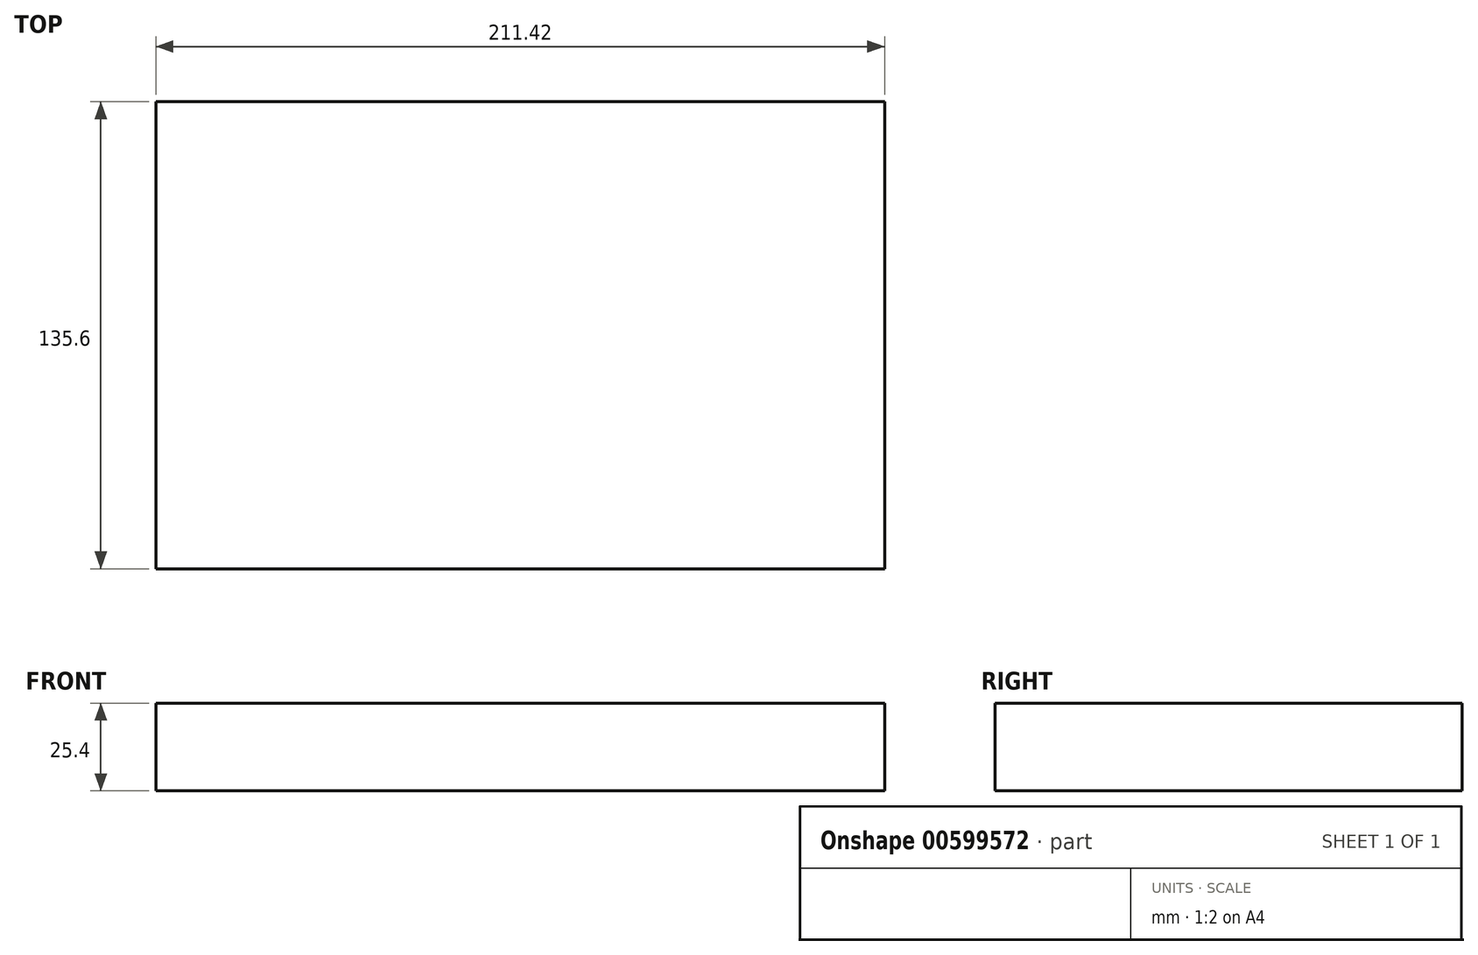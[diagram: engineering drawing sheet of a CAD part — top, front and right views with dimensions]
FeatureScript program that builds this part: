
annotation { "Feature Type Name" : "Feature", "Feature Type Description" : "" }
export const myFeature = defineFeature(function(context is Context, id is Id, definition is map)
    precondition{}
    {
        {
            var Q0;
            Q0=qCreatedBy(makeId("Top.planeOp"),FACE);
            var sketch = newSketch(context, id + "F0", { "sketchPlane" : qUnion([Q0])});
            skLineSegment(sketch, "E0.bottom", {"start": v(-105.71, 67.8) * mm, "end": v(105.71, 67.8) * mm});
            skLineSegment(sketch, "E0.top", {"start": v(-105.71, -67.8) * mm, "end": v(105.71, -67.8) * mm});
            skLineSegment(sketch, "E0.left", {"start": v(-105.71, 67.8) * mm, "end": v(-105.71, -67.8) * mm});
            skLineSegment(sketch, "E0.right", {"start": v(105.71, 67.8) * mm, "end": v(105.71, -67.8) * mm});
            skPoint(sketch, "E0.middle", {"position": v(0, 0) * mm});
            skSolve(sketch);
        }
        {
            var Q0;
            Q0=makeQuery(id+"F0.imprint","IMPRINT",FACE,{"disambiguationData":[TD([[makeQuery(id+"F0.imprint","IMPRINT",EDGE,{"derivedFrom":sQuery(id+"F0.wireOp",EDGE,"E0.bottom")}),-1.0]])]});
            extrude(context, id + "F1", {"entities" : qUnion([Q0]), "depth" : 25.4 * mm, "offsetDistance" : 25.4 * mm});
        }
    });
